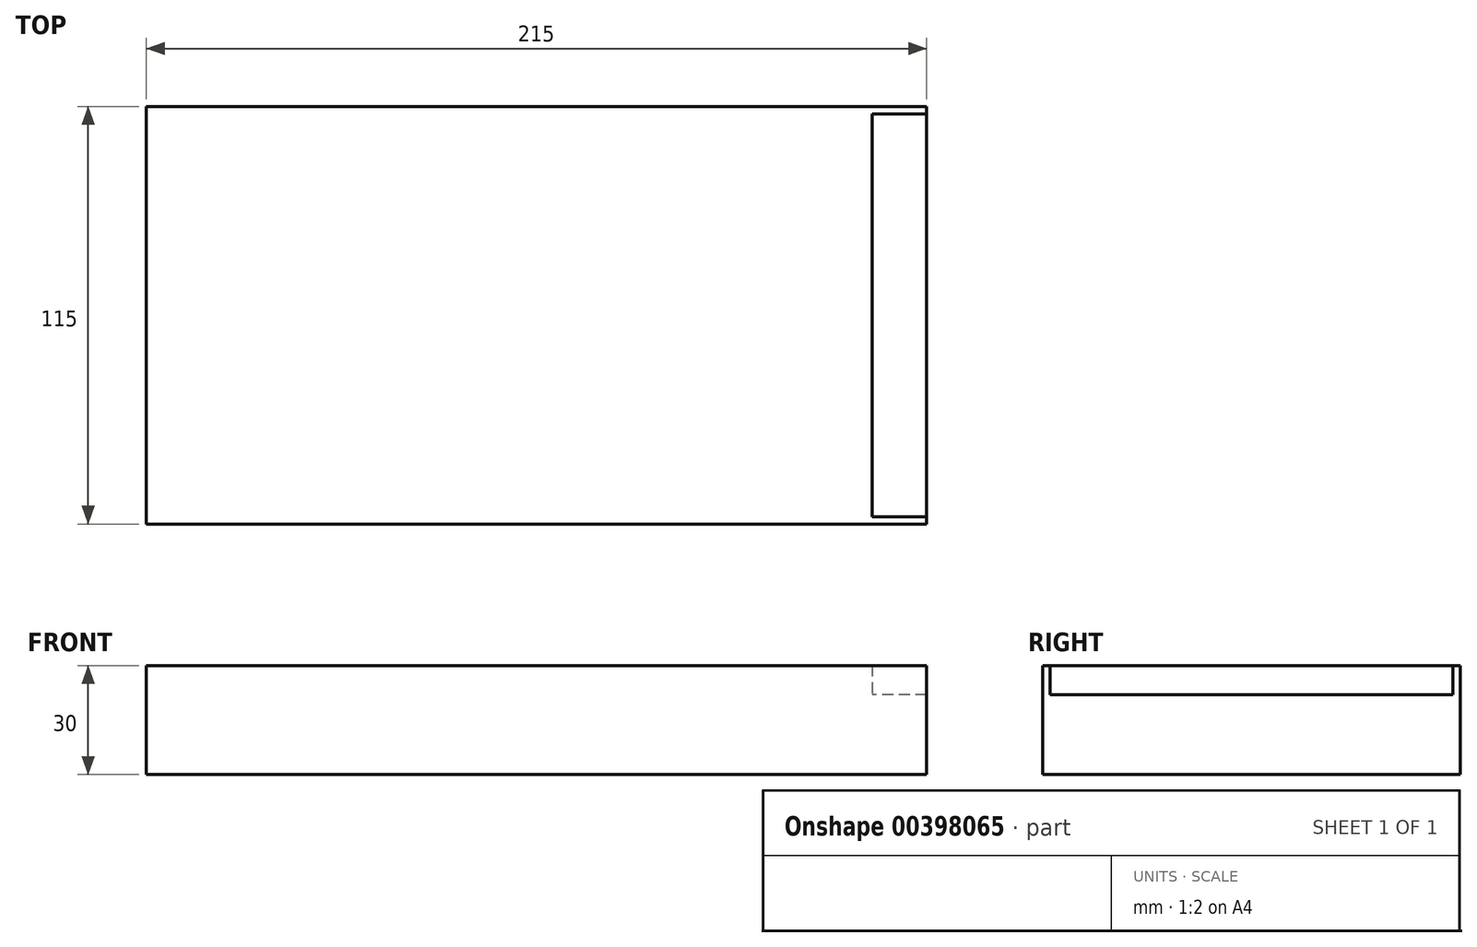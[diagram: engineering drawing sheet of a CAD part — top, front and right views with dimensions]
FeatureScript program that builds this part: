
annotation { "Feature Type Name" : "Feature", "Feature Type Description" : "" }
export const myFeature = defineFeature(function(context is Context, id is Id, definition is map)
    precondition{}
    {
        {
            var Q0;
            Q0=qCreatedBy(makeId("Top.planeOp"),FACE);
            var sketch = newSketch(context, id + "F0", { "sketchPlane" : qUnion([Q0])});
            skLineSegment(sketch, "E0.bottom", {"start": v(0, 0) * mm, "end": v(215, 0) * mm});
            skLineSegment(sketch, "E0.top", {"start": v(0, 115) * mm, "end": v(215, 115) * mm});
            skLineSegment(sketch, "E0.left", {"start": v(0, 0) * mm, "end": v(0, 115) * mm});
            skLineSegment(sketch, "E0.right", {"start": v(215, 0) * mm, "end": v(215, 115) * mm});
            skLineSegment(sketch, "E1", {"start": v(200, 113) * mm, "end": v(200, 2) * mm});
            skLineSegment(sketch, "E2", {"start": v(215, 2) * mm, "end": v(200, 2) * mm});
            skLineSegment(sketch, "E3", {"start": v(215, 113) * mm, "end": v(200, 113) * mm});
            skLineSegment(sketch, "E4", {"start": v(207.5, 2) * mm, "end": v(207.5, 0) * mm, "construction": true});
            skLineSegment(sketch, "E5", {"start": v(207.5, 113) * mm, "end": v(207.5, 115) * mm, "construction": true});
            skSolve(sketch);
        }
        {
            var Q0;
            {var subQ0=sQuery(id+"F0.wireOp",EDGE,"E0.left");Q0=makeQuery(id+"F0.imprint","IMPRINT",FACE,{"disambiguationData":[TD([[makeQuery(id+"F0.imprint","IMPRINT",EDGE,{"derivedFrom":subQ0}),-1.0]])]});}
            extrude(context, id + "F1", {"entities" : qUnion([Q0]), "depth" : 30 * mm});
        }
        {
            var Q0;
            Q0=makeQuery(id+"F0.imprint","IMPRINT",FACE,{"disambiguationData":[TD([[makeQuery(id+"F0.imprint","IMPRINT",EDGE,{"derivedFrom":sQuery(id+"F0.wireOp",EDGE,"E1")}),1.0]])]});
            extrude(context, id + "F2", {"entities" : qUnion([Q0]), "operationType" : NewBodyOperationType.ADD, "depth" : 22 * mm});
        }
    });
